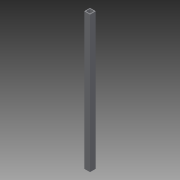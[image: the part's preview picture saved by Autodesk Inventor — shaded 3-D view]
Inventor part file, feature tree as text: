
AUTODESK INVENTOR PART (.ipt)
format: ipt  version: 2013 (Build 170138000, 138)  size: 71,680 bytes
history: native  units: in
note: dims shown in document units (in); Inventor stores cm internally (conversion verified against a paired STEP export)
features: extrude x1, sketch x1
ambient origin geometry x8: Origin, YZ Plane, XZ Plane, XY Plane, X Axis, Y Axis, Z Axis, Center Point
bodies: Solid1 (feature_tree)
feature tree (2):
  extrude  "Extrusion1"  Depth=1.0in
  sketch  "Sketch1"  dims[d0=1.0in d1=1.0in d2=0.75in d3=0.75in d4=24.0in d5=0.0in]
